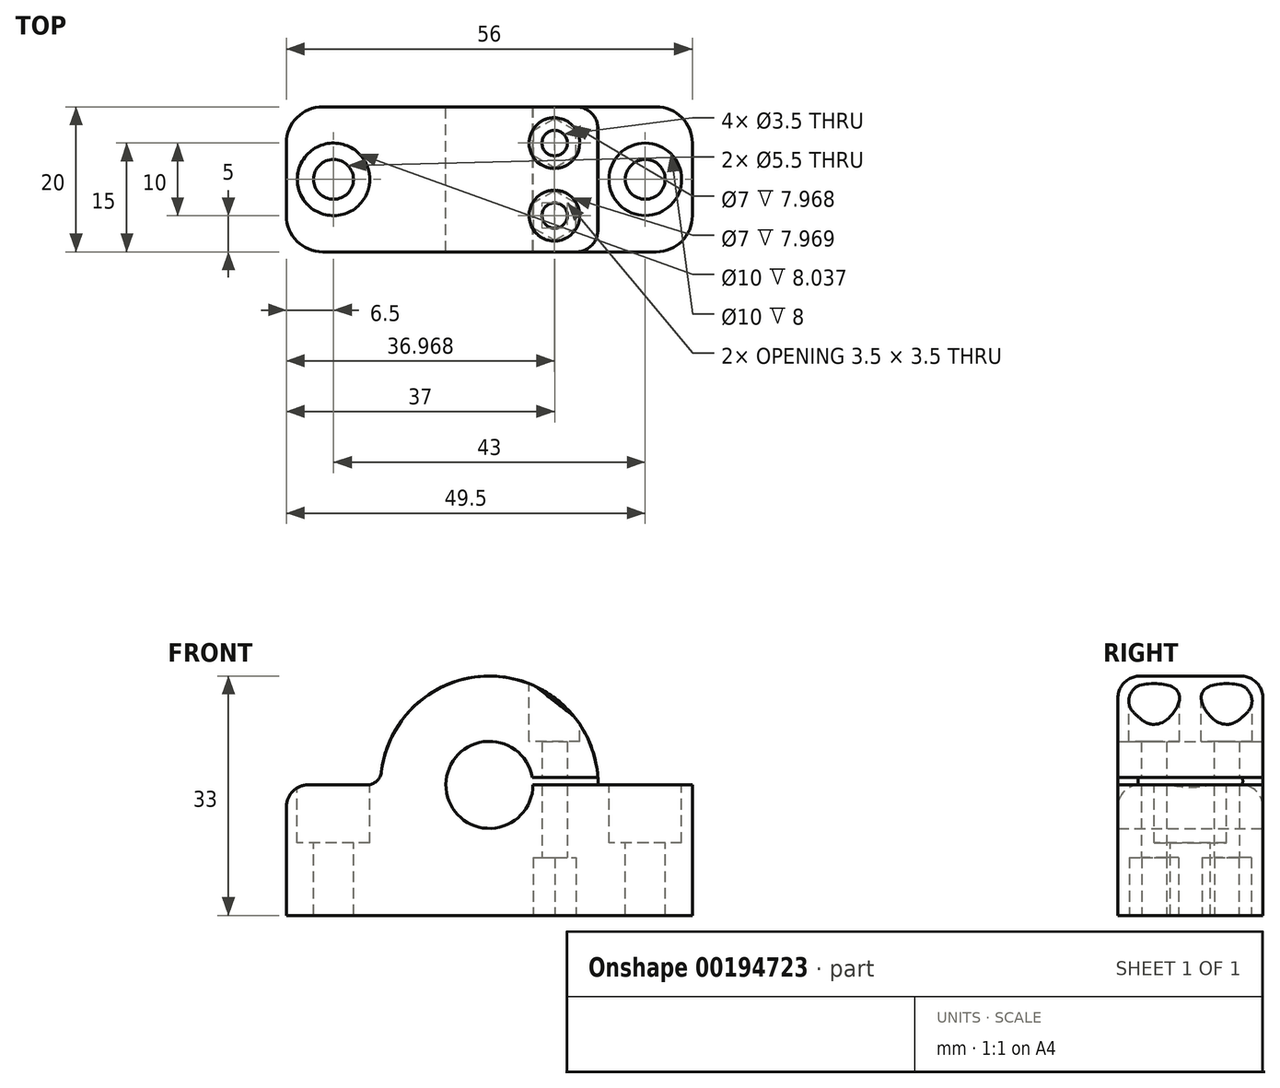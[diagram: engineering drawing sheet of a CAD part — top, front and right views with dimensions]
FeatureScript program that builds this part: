
annotation { "Feature Type Name" : "Feature", "Feature Type Description" : "" }
export const myFeature = defineFeature(function(context is Context, id is Id, definition is map)
    precondition{}
    {
        {
            var Q0;
            Q0=qCreatedBy(makeId("Front.planeOp"),FACE);
            var sketch = newSketch(context, id + "F0", { "sketchPlane" : qUnion([Q0])});
            skLineSegment(sketch, "E0", {"start": v(0, 0) * mm, "end": v(46, 0) * mm});
            skLineSegment(sketch, "E1", {"start": v(46, 18) * mm, "end": v(38, 18) * mm});
            skLineSegment(sketch, "E2", {"start": v(23, 2.03) * mm, "end": v(23, 12) * mm});
            skCircle(sketch, "E3", {"center": v(23, 18) * mm, "radius": 6 * mm});
            skArc(sketch, "E4", {"start": v(38, 18) * mm, "mid": v(23, 33) * mm, "end": v(8, 18) * mm});
            skPoint(sketch, "E5.orphan", {"position": v(23, 0) * mm});
            skLineSegment(sketch, "E6.trimOffspring", {"start": v(8, 18) * mm, "end": v(0, 18) * mm});
            skLineSegment(sketch, "E7", {"start": v(0, 18) * mm, "end": v(-5, 18) * mm});
            skLineSegment(sketch, "E8", {"start": v(-5, 18) * mm, "end": v(-5, 0) * mm});
            skLineSegment(sketch, "E9", {"start": v(-5, 0) * mm, "end": v(0, 0) * mm});
            skLineSegment(sketch, "E10", {"start": v(46, 18) * mm, "end": v(51, 18) * mm});
            skLineSegment(sketch, "E11", {"start": v(51, 18) * mm, "end": v(51, 0) * mm});
            skLineSegment(sketch, "E12", {"start": v(51, 0) * mm, "end": v(46, 0) * mm});
            skSolve(sketch);
        }
        {
            var Q0;
            Q0 = qSketchRegion(id + "F0", true);
            extrude(context, id + "F1", {"entities" : qUnion([Q0]), "depth" : 20 * mm});
        }
        {
            var Q0;
            Q0=makeQuery(id+"F1.opExtrude","CAP_FACE",FACE,{"disambiguationData":[OSD([sQuery(id+"F0.wireOp",EDGE,"E0"),sQuery(id+"F0.wireOp",EDGE,"THL3Rdyr-WuDa-PEdF-Rsy6-Ql4hvmJiIkfp"),sQuery(id+"F0.wireOp",EDGE,"E1"),sQuery(id+"F0.wireOp",EDGE,"PfEdIOGx-NsgI-H07u-bir1-d25Lm9cwLRIb"),sQuery(id+"F0.wireOp",EDGE,"E3"),sQuery(id+"F0.wireOp",EDGE,"E4"),sQuery(id+"F0.wireOp",EDGE,"E6.trimOffspring")])],"isStart":false});
            var sketch = newSketch(context, id + "F2", { "sketchPlane" : qUnion([Q0])});
            skLineSegment(sketch, "E13", {"start": v(38, 18) * mm, "end": v(29, 18) * mm});
            skLineSegment(sketch, "E14", {"start": v(29, 18) * mm, "end": v(28.9, 19.04) * mm});
            skLineSegment(sketch, "E15", {"start": v(28.9, 19.04) * mm, "end": v(37.96, 19.04) * mm});
            skLineSegment(sketch, "E16", {"start": v(37.96, 19.04) * mm, "end": v(38, 18) * mm});
            skSolve(sketch);
        }
        {
            var Q0;
            Q0=makeQuery(id+"F1.opExtrude","SWEPT_FACE",FACE,{"disambiguationData":[OSD([sQuery(id+"F0.wireOp",EDGE,"E6.trimOffspring")])]});
            var sketch = newSketch(context, id + "F3", { "sketchPlane" : qUnion([Q0])});
            skPoint(sketch, "E17.endSnap0", {"position": v(8, -10) * mm});
            skCircle(sketch, "E18", {"center": v(1.5, -10) * mm, "radius": 2.75 * mm});
            skSolve(sketch);
        }
        {
            var Q0;
            Q0=makeQuery(id+"FKNmM5ujoBkWRs0_1.boolean.opBoolean","MERGE",FACE,{"derivedFrom":[makeQuery(id+"F1.opExtrude","SWEPT_FACE",FACE,{"disambiguationData":[OSD([sQuery(id+"F0.wireOp",EDGE,"E1")])]}),makeQuery(id+"FKNmM5ujoBkWRs0_1.opExtrude","SWEPT_FACE",FACE,{"disambiguationData":[OSD([sQuery(id+"F2.wireOp",EDGE,"D8yx7LVh-9Jys-sex7-rBta-GiDwl0LXf01W")])]})]});
            var sketch = newSketch(context, id + "F4", { "sketchPlane" : qUnion([Q0])});
            skCircle(sketch, "E19", {"center": v(44.5, -10) * mm, "radius": 2.75 * mm});
            skSolve(sketch);
        }
        {
            var Q0;
            Q0=makeQuery(id+"F4.imprint","IMPRINT",FACE,{"disambiguationData":[TD([[makeQuery(id+"F4.imprint","IMPRINT",EDGE,{"derivedFrom":sQuery(id+"F4.wireOp",EDGE,"E19")}),1.0]])]});
            extrude(context, id + "F5", {"entities" : qUnion([Q0]), "operationType" : NewBodyOperationType.REMOVE, "oppositeDirection" : true, "depth" : 25 * mm});
        }
        {
            var Q0;
            Q0=makeQuery(id+"F1.opExtrude","SWEPT_FACE",FACE,{"disambiguationData":[OSD([sQuery(id+"F0.wireOp",EDGE,"E0")])]});
            var sketch = newSketch(context, id + "F6", { "sketchPlane" : qUnion([Q0])});
            skLineSegment(sketch, "E20", {"start": v(46, 20) * mm, "end": v(32, 20) * mm});
            skLineSegment(sketch, "E21", {"start": v(32, 20) * mm, "end": v(32, 15) * mm});
            skLineSegment(sketch, "E22", {"start": v(32, 15) * mm, "end": v(32, 5) * mm});
            skCircle(sketch, "E23", {"center": v(32, 15) * mm, "radius": 1.75 * mm});
            skCircle(sketch, "E24", {"center": v(32, 5) * mm, "radius": 1.75 * mm});
            skSolve(sketch);
        }
        {
            var Q0;
            Q0=makeQuery(id+"F6.imprint","IMPRINT",FACE,{"disambiguationData":[TD([[makeQuery(id+"F6.imprint","IMPRINT",EDGE,{"derivedFrom":sQuery(id+"F6.wireOp",EDGE,"E24")}),1.0]])]});
            var Q1;
            {var subQ0=sQuery(id+"F6.wireOp",EDGE,"E22");var subQ1=sQuery(id+"F6.wireOp",EDGE,"E21");var subQ2=makeQuery(id+"F6.imprint","INTERSECT",VERTEX,{"derivedFrom":[subQ1,subQ0]});Q1=makeQuery(id+"F6.imprint","IMPRINT",FACE,{"disambiguationData":[TD([[makeQuery(id+"F6.imprint","IMPRINT",EDGE,{"disambiguationData":[TD([[subQ2,1.0]])],"derivedFrom":subQ1}),-1.0]])]});}
            var Q2;
            {var subQ0=sQuery(id+"F6.wireOp",EDGE,"E22");var subQ1=sQuery(id+"F6.wireOp",EDGE,"E21");var subQ2=makeQuery(id+"F6.imprint","INTERSECT",VERTEX,{"derivedFrom":[subQ1,subQ0]});Q2=makeQuery(id+"F6.imprint","IMPRINT",FACE,{"disambiguationData":[TD([[makeQuery(id+"F6.imprint","IMPRINT",EDGE,{"disambiguationData":[TD([[subQ2,1.0]])],"derivedFrom":subQ1}),1.0]])]});}
            extrude(context, id + "F7", {"entities" : qUnion([Q0, Q1, Q2]), "operationType" : NewBodyOperationType.REMOVE, "oppositeDirection" : true, "depth" : 25 * mm});
        }
        {
            var Q0;
            Q0=makeQuery(id+"FKNmM5ujoBkWRs0_1.boolean.opBoolean","MERGE",FACE,{"derivedFrom":[makeQuery(id+"F1.opExtrude","SWEPT_FACE",FACE,{"disambiguationData":[OSD([sQuery(id+"F0.wireOp",EDGE,"E1")])]}),makeQuery(id+"FKNmM5ujoBkWRs0_1.opExtrude","SWEPT_FACE",FACE,{"disambiguationData":[OSD([sQuery(id+"F2.wireOp",EDGE,"D8yx7LVh-9Jys-sex7-rBta-GiDwl0LXf01W")])]})]});
            cPlane(context, id + "F8", {"entities" : qUnion([Q0]), "cplaneType" : CPlaneType.OFFSET, "offset" : 20 * mm, "width" : 150 * mm, "height" : 150 * mm});
        }
        {
            var Q0;
            Q0=qCreatedBy(id+"F8.planeOp",FACE);
            var sketch = newSketch(context, id + "F9", { "sketchPlane" : qUnion([Q0])});
            skCircle(sketch, "E25", {"center": v(31.97, -5) * mm, "radius": 3.5 * mm});
            skCircle(sketch, "E26", {"center": v(31.97, -15) * mm, "radius": 3.5 * mm});
            skSolve(sketch);
        }
        {
            var Q0;
            Q0=makeQuery(id+"F9.imprint","IMPRINT",FACE,{"disambiguationData":[TD([[makeQuery(id+"F9.imprint","IMPRINT",EDGE,{"derivedFrom":sQuery(id+"F9.wireOp",EDGE,"E25")}),1.0]])]});
            var Q1;
            Q1=makeQuery(id+"F9.imprint","IMPRINT",FACE,{"disambiguationData":[TD([[makeQuery(id+"F9.imprint","IMPRINT",EDGE,{"derivedFrom":sQuery(id+"F9.wireOp",EDGE,"E26")}),1.0]])]});
            extrude(context, id + "F10", {"entities" : qUnion([Q0, Q1]), "operationType" : NewBodyOperationType.REMOVE, "oppositeDirection" : true, "depth" : 14 * mm});
        }
        {
            var Q0;
            Q0=makeQuery(id+"F1.opExtrude","SWEPT_FACE",FACE,{"disambiguationData":[OSD([sQuery(id+"F0.wireOp",EDGE,"E0")])]});
            var sketch = newSketch(context, id + "F11", { "sketchPlane" : qUnion([Q0])});
            skCircle(sketch, "E27.cCircle", {"center": v(32, 15) * mm, "radius": 2.94 * mm, "construction": true});
            skLineSegment(sketch, "E27.0", {"start": v(34.94, 16.7) * mm, "end": v(34.94, 13.3) * mm});
            skLineSegment(sketch, "E27.1", {"start": v(34.94, 13.3) * mm, "end": v(32, 11.6) * mm});
            skLineSegment(sketch, "E27.2", {"start": v(32, 11.6) * mm, "end": v(29.06, 13.3) * mm});
            skLineSegment(sketch, "E27.3", {"start": v(29.06, 13.3) * mm, "end": v(29.06, 16.7) * mm});
            skLineSegment(sketch, "E27.4", {"start": v(29.06, 16.7) * mm, "end": v(32, 18.4) * mm});
            skLineSegment(sketch, "E27.5", {"start": v(32, 18.4) * mm, "end": v(34.94, 16.7) * mm});
            skPoint(sketch, "E27.0.midPoint", {"position": v(34.94, 15) * mm});
            skCircle(sketch, "E28.cCircle", {"center": v(32, 5) * mm, "radius": 2.94 * mm, "construction": true});
            skLineSegment(sketch, "E28.0", {"start": v(34.94, 6.7) * mm, "end": v(34.94, 3.3) * mm});
            skLineSegment(sketch, "E28.1", {"start": v(34.94, 3.3) * mm, "end": v(32, 1.6) * mm});
            skLineSegment(sketch, "E28.2", {"start": v(32, 1.6) * mm, "end": v(29.06, 3.3) * mm});
            skLineSegment(sketch, "E28.3", {"start": v(29.06, 3.3) * mm, "end": v(29.06, 6.7) * mm});
            skLineSegment(sketch, "E28.4", {"start": v(29.06, 6.7) * mm, "end": v(32, 8.4) * mm});
            skLineSegment(sketch, "E28.5", {"start": v(32, 8.4) * mm, "end": v(34.94, 6.7) * mm});
            skPoint(sketch, "E28.0.midPoint", {"position": v(34.94, 5) * mm});
            skCircle(sketch, "E29", {"center": v(32, 15) * mm, "radius": 3.4 * mm});
            skCircle(sketch, "E30", {"center": v(32, 5) * mm, "radius": 3.4 * mm});
            skSolve(sketch);
        }
        {
            var Q0;
            Q0=makeQuery(id+"F11.imprint","IMPRINT",FACE,{"disambiguationData":[TD([[makeQuery(id+"F11.imprint","IMPRINT",EDGE,{"derivedFrom":sQuery(id+"F11.wireOp",EDGE,"E28.0")}),-1.0]])]});
            var Q1;
            Q1=makeQuery(id+"F11.imprint","IMPRINT",FACE,{"disambiguationData":[TD([[makeQuery(id+"F11.imprint","IMPRINT",EDGE,{"derivedFrom":sQuery(id+"F11.wireOp",EDGE,"E27.0")}),-1.0]])]});
            extrude(context, id + "F12", {"entities" : qUnion([Q0, Q1]), "operationType" : NewBodyOperationType.REMOVE, "oppositeDirection" : true, "depth" : 8 * mm});
        }
        {
            var Q0;
            Q0=makeQuery(id+"F1.opExtrude","CAP_EDGE",EDGE,{"disambiguationData":[OSD([sQuery(id+"F0.wireOp",EDGE,"E8")])],"isStart":false});
            var Q1;
            Q1=makeQuery(id+"F1.opExtrude","CAP_EDGE",EDGE,{"disambiguationData":[OSD([sQuery(id+"F0.wireOp",EDGE,"E11")])],"isStart":false});
            var Q2;
            Q2=makeQuery(id+"F1.opExtrude","CAP_EDGE",EDGE,{"disambiguationData":[OSD([sQuery(id+"F0.wireOp",EDGE,"E11")])],"isStart":true});
            var Q3;
            Q3=makeQuery(id+"F1.opExtrude","CAP_EDGE",EDGE,{"disambiguationData":[OSD([sQuery(id+"F0.wireOp",EDGE,"E8")])],"isStart":true});
            fillet(context, id + "F13", {"entities" : qUnion([Q0, Q1, Q2, Q3]), "radius" : 5 * mm, "tangentPropagation" : true, "allowEdgeOverflow" : false});
        }
        {
            var Q0;
            Q0=makeQuery(id+"F1.opExtrude","CAP_EDGE",EDGE,{"disambiguationData":[OSD([sQuery(id+"F0.wireOp",EDGE,"E4")])],"isStart":false});
            var Q1;
            Q1=makeQuery(id+"F1.opExtrude","CAP_EDGE",EDGE,{"disambiguationData":[OSD([sQuery(id+"F0.wireOp",EDGE,"E4")])],"isStart":true});
            fillet(context, id + "F14", {"entities" : qUnion([Q0, Q1]), "radius" : 3 * mm, "tangentPropagation" : true, "allowEdgeOverflow" : false});
        }
        {
            var Q0;
            Q0=makeQuery(id+"F1.opExtrude","SWEPT_EDGE",EDGE,{"disambiguationData":[OSD([sQuery(id+"F0.wireOp",EDGE,"PfEdIOGx-NsgI-H07u-bir1-d25Lm9cwLRIb"),sQuery(id+"F0.wireOp",EDGE,"E6.trimOffspring")])]});
            fillet(context, id + "F15", {"entities" : qUnion([Q0]), "radius" : 2 * mm, "tangentPropagation" : true, "allowEdgeOverflow" : false});
        }
        {
            var Q0;
            Q0=makeQuery(id+"F3.imprint","IMPRINT",FACE,{"disambiguationData":[TD([[makeQuery(id+"F3.imprint","IMPRINT",EDGE,{"derivedFrom":sQuery(id+"F3.wireOp",EDGE,"E18")}),1.0]])]});
            extrude(context, id + "F16", {"entities" : qUnion([Q0]), "operationType" : NewBodyOperationType.REMOVE, "oppositeDirection" : true, "depth" : 25 * mm});
        }
        {
            var Q0;
            Q0=makeQuery(id+"F1.opExtrude","SWEPT_FACE",FACE,{"disambiguationData":[OSD([sQuery(id+"F0.wireOp",EDGE,"E6.trimOffspring")])]});
            var sketch = newSketch(context, id + "F17", { "sketchPlane" : qUnion([Q0])});
            skCircle(sketch, "E31", {"center": v(1.5, -10) * mm, "radius": 5 * mm});
            skSolve(sketch);
        }
        {
            var Q0;
            Q0 = qSketchRegion(id + "F17", true);
            extrude(context, id + "F18", {"entities" : qUnion([Q0]), "operationType" : NewBodyOperationType.REMOVE, "oppositeDirection" : true, "depth" : 8 * mm});
        }
        {
            var Q0;
            {var subQ0=sQuery(id+"F0.wireOp",EDGE,"E6.trimOffspring");var subQ2=makeQuery(id+"F1.opExtrude","SWEPT_FACE",FACE,{"disambiguationData":[OSD([subQ0])]});var subQ3=sQuery(id+"F0.wireOp",EDGE,"E4");Q0=makeQuery(id+"F18.boolean.opBoolean","SPLIT",FACE,{"disambiguationData":[TD([makeQuery(id+"F14.opFillet","BLEND_FACE",FACE,{"disambiguationData":[OSD([subQ3]),TDD([makeQuery(id+"F1.opExtrude","CAP_EDGE",EDGE,{"disambiguationData":[OSD([subQ3])],"isStart":false})])]})])],"derivedFrom":subQ2});}
            var sketch = newSketch(context, id + "F19", { "sketchPlane" : qUnion([Q0])});
            skCircle(sketch, "E32", {"center": v(1.5, -10) * mm, "radius": 5 * mm});
            skSolve(sketch);
        }
        {
            var Q0;
            Q0 = qSketchRegion(id + "F19", true);
            extrude(context, id + "F20", {"entities" : qUnion([Q0]), "operationType" : NewBodyOperationType.REMOVE, "depth" : 10 * mm});
        }
        {
            var Q0;
            Q0=makeQuery(id+"F1.opExtrude","SWEPT_FACE",FACE,{"disambiguationData":[OSD([sQuery(id+"F0.wireOp",EDGE,"E1")])]});
            var sketch = newSketch(context, id + "F21", { "sketchPlane" : qUnion([Q0])});
            skCircle(sketch, "E33", {"center": v(44.5, -10) * mm, "radius": 5 * mm});
            skSolve(sketch);
        }
        {
            var Q0;
            {var subQ0=sQuery(id+"F4.wireOp",EDGE,"E19");var subQ1=makeQuery(id+"F5.boolean.opBoolean","COPY",EDGE,{"derivedFrom":makeQuery(id+"F5.opExtrude","CAP_EDGE",EDGE,{"disambiguationData":[OSD([subQ0])],"isStart":true})});Q0=makeQuery(id+"F21.imprint","IMPRINT",FACE,{"disambiguationData":[TD([[makeQuery(id+"F21.imprint","IMPRINT",EDGE,{"derivedFrom":subQ1}),-1.0]])]});}
            var Q1;
            {var subQ0=sQuery(id+"F21.wireOp",EDGE,"E33");var subQ1=sQuery(id+"F0.wireOp",EDGE,"E6.trimOffspring");var subQ2=sQuery(id+"F0.wireOp",EDGE,"E4");var subQ3=sQuery(id+"F0.wireOp",EDGE,"E3");var subQ4=sQuery(id+"F0.wireOp",EDGE,"PfEdIOGx-NsgI-H07u-bir1-d25Lm9cwLRIb");var subQ5=sQuery(id+"F0.wireOp",EDGE,"E1");var subQ6=sQuery(id+"F0.wireOp",EDGE,"THL3Rdyr-WuDa-PEdF-Rsy6-Ql4hvmJiIkfp");var subQ7=sQuery(id+"F0.wireOp",EDGE,"E0");var subQ12=makeQuery(id+"F1.opExtrude","SWEPT_EDGE",EDGE,{"disambiguationData":[OSD([subQ5,subQ2])]});var subQ13=makeQuery(id+"F5.boolean.opBoolean","SPLIT",EDGE,{"disambiguationData":[TD([makeQuery(id+"F1.opExtrude","CAP_FACE",FACE,{"disambiguationData":[OSD([subQ7,subQ6,subQ5,subQ4,subQ3,subQ2,subQ1])],"isStart":true})])],"derivedFrom":subQ12});var subQ14=makeQuery(id+"F21.imprint","INTERSECT",VERTEX,{"derivedFrom":[subQ13,subQ0]});Q1=makeQuery(id+"F21.imprint","IMPRINT",FACE,{"disambiguationData":[TD([[makeQuery(id+"F21.imprint","IMPRINT",EDGE,{"disambiguationData":[TD([[subQ14,-1.0]])],"derivedFrom":subQ0}),1.0]])]});}
            var Q2;
            {var subQ0=sQuery(id+"F21.wireOp",EDGE,"E33");var subQ1=sQuery(id+"F0.wireOp",EDGE,"E1");var subQ2=makeQuery(id+"F15.opFillet","BLEND_EDGE",EDGE,{"blendedFrom":[makeQuery(id+"F1.opExtrude","SWEPT_EDGE",EDGE,{"disambiguationData":[OSD([sQuery(id+"F0.wireOp",EDGE,"THL3Rdyr-WuDa-PEdF-Rsy6-Ql4hvmJiIkfp"),subQ1])]}),makeQuery(id+"F1.opExtrude","SWEPT_FACE",FACE,{"disambiguationData":[OSD([subQ1])]})],"blendedInto":[makeQuery(id+"F1.opExtrude","SWEPT_FACE",FACE,{"disambiguationData":[OSD([subQ1])]})]});var subQ3=makeQuery(id+"F21.imprint","INTERSECT",VERTEX,{"disambiguationData":[OD(0.0)],"derivedFrom":[subQ2,subQ0]});Q2=makeQuery(id+"F21.imprint","IMPRINT",FACE,{"disambiguationData":[TD([[makeQuery(id+"F21.imprint","IMPRINT",EDGE,{"disambiguationData":[TD([[subQ3,1.0]])],"derivedFrom":subQ0}),1.0]])]});}
            var Q3;
            Q3=sQuery(id+"F21.wireOp",EDGE,"E33");
            extrude(context, id + "F22", {"entities" : qUnion([Q0, Q1, Q2]), "operationType" : NewBodyOperationType.REMOVE, "surfaceEntities" : qUnion([Q3]), "oppositeDirection" : true, "depth" : 8 * mm});
        }
        {
            var Q0;
            {var subQ0=sQuery(id+"F0.wireOp",EDGE,"E1");var subQ1=makeQuery(id+"F1.opExtrude","SWEPT_FACE",FACE,{"disambiguationData":[OSD([subQ0])]});var subQ3=sQuery(id+"F0.wireOp",EDGE,"E4");Q0=makeQuery(id+"F22.boolean.opBoolean","SPLIT",FACE,{"disambiguationData":[TD([makeQuery(id+"F14.opFillet","BLEND_FACE",FACE,{"disambiguationData":[OSD([subQ3]),TDD([makeQuery(id+"F1.opExtrude","CAP_EDGE",EDGE,{"disambiguationData":[OSD([subQ3])],"isStart":true})])]})])],"derivedFrom":subQ1});}
            var sketch = newSketch(context, id + "F23", { "sketchPlane" : qUnion([Q0])});
            skCircle(sketch, "E34", {"center": v(44.5, -10) * mm, "radius": 5 * mm});
            skSolve(sketch);
        }
        {
            var Q0;
            {var subQ0=sQuery(id+"F23.wireOp",EDGE,"E34");var subQ2=sQuery(id+"F0.wireOp",EDGE,"E1");var subQ3=sQuery(id+"F0.wireOp",EDGE,"THL3Rdyr-WuDa-PEdF-Rsy6-Ql4hvmJiIkfp");var subQ4=makeQuery(id+"F1.opExtrude","SWEPT_FACE",FACE,{"disambiguationData":[OSD([subQ2])]});var subQ6=makeQuery(id+"F1.opExtrude","SWEPT_EDGE",EDGE,{"disambiguationData":[OSD([subQ3,subQ2])]});var subQ7=subQ4;var subQ8=makeQuery(id+"F23.imprint","INTERSECT",VERTEX,{"derivedFrom":[makeQuery(id+"F22.boolean.opBoolean","SPLIT",EDGE,{"disambiguationData":[TD([makeQuery(id+"F15.opFillet","BLEND_FACE",FACE,{"disambiguationData":[OSD([subQ3,subQ2]),TDD([makeQuery(id+"F13.opFillet","BLEND_EDGE",EDGE,{"blendedFrom":[makeQuery(id+"F1.opExtrude","CAP_EDGE",EDGE,{"disambiguationData":[OSD([subQ3])],"isStart":true}),subQ7],"blendedInto":[subQ7]})])]})])],"derivedFrom":makeQuery(id+"F15.opFillet","BLEND_EDGE",EDGE,{"blendedFrom":[subQ6,subQ7],"blendedInto":[subQ7]})}),subQ0]});Q0=makeQuery(id+"F23.imprint","IMPRINT",FACE,{"disambiguationData":[TD([[makeQuery(id+"F23.imprint","IMPRINT",EDGE,{"disambiguationData":[TD([[subQ8,-1.0]])],"derivedFrom":subQ0}),1.0]])]});}
            var Q1;
            Q1=sQuery(id+"F23.wireOp",EDGE,"E34");
            extrude(context, id + "F24", {"entities" : qUnion([Q0]), "operationType" : NewBodyOperationType.REMOVE, "surfaceEntities" : qUnion([Q1]), "depth" : 10 * mm});
        }
        {
            var Q0;
            {var subQ0=sQuery(id+"F2.wireOp",EDGE,"E13");Q0=makeQuery(id+"F2.imprint","IMPRINT",FACE,{"disambiguationData":[TD([[makeQuery(id+"F2.imprint","IMPRINT",EDGE,{"derivedFrom":subQ0}),-1.0]])]});}
            extrude(context, id + "F25", {"entities" : qUnion([Q0]), "operationType" : NewBodyOperationType.REMOVE, "oppositeDirection" : true, "depth" : 25 * mm});
        }
        {
            var Q0;
            Q0=makeQuery(id+"F1.opExtrude","CAP_EDGE",EDGE,{"disambiguationData":[OSD([sQuery(id+"F0.wireOp",EDGE,"E6.trimOffspring"),sQuery(id+"F0.wireOp",EDGE,"E7")])],"isStart":false});
            var Q1;
            Q1=makeQuery(id+"F25.boolean.opBoolean","MERGE",EDGE,{"derivedFrom":[makeQuery(id+"F1.opExtrude","CAP_EDGE",EDGE,{"disambiguationData":[OSD([sQuery(id+"F0.wireOp",EDGE,"E1"),sQuery(id+"F0.wireOp",EDGE,"E10")])],"isStart":false}),makeQuery(id+"F25.opExtrude","CAP_EDGE",EDGE,{"disambiguationData":[OSD([sQuery(id+"F2.wireOp",EDGE,"E13")])],"isStart":true})]});
            fillet(context, id + "F26", {"entities" : qUnion([Q0, Q1]), "radius" : 3 * mm, "tangentPropagation" : true, "allowEdgeOverflow" : false});
        }
    });
